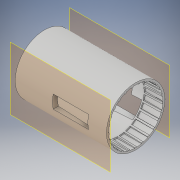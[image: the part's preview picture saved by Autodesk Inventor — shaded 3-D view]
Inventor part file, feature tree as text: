
AUTODESK INVENTOR PART (.ipt)
format: ipt  version: 2019.1 (Build 231200000, 200)  size: 846,336 bytes
history: native  units: mm
features: sketch x5, extrude x4, plane x2, revolve x1
ambient origin geometry x8: Origin, YZ Plane, XZ Plane, XY Plane, X Axis, Y Axis, Z Axis, Center Point
bodies: Solid1 (feature_tree)
feature tree (12):
  revolve  "Revolution1"  [1 undecoded]
  extrude  "Extrusion1"  Depth=1.0mm TaperAngle=360.0deg
  plane  "Work Plane1"
  extrude  "Extrusion2"  Depth=12.0mm
  plane  "Work Plane2"
  extrude  "Extrusion3"  Depth=5.3mm
  extrude  "Extrusion4"  Depth=1.0mm
  sketch  "Sketch1"  dims[d3=90.0deg d4=2.0mm]
  sketch  "Sketch2"  dims[d5=1.0mm d6=250.0mm d8=360.0deg]
  sketch  "Sketch3"  dims[d10=7.0mm d11=0.0mm d12=12.0mm]
  sketch  "Sketch4"  dims[d13=14.25mm d14=5.3mm]
  sketch  "Sketch5"  dims[d15=2.65mm d16=7.5mm d17=10.0mm d18=0.0mm d19=-24.0mm d25=10.0mm d26=0.0mm d27=1.0mm d28=0.0mm d29=9.0mm d30=3.0mm d31=27.925268mm d32=3.0mm d33=27.925268mm]
note: 1 required parameter value undecoded (feature->parameter linkage not recoverable at this tier; creation-order binding heuristic only, values carry confidence <= 0.55)
